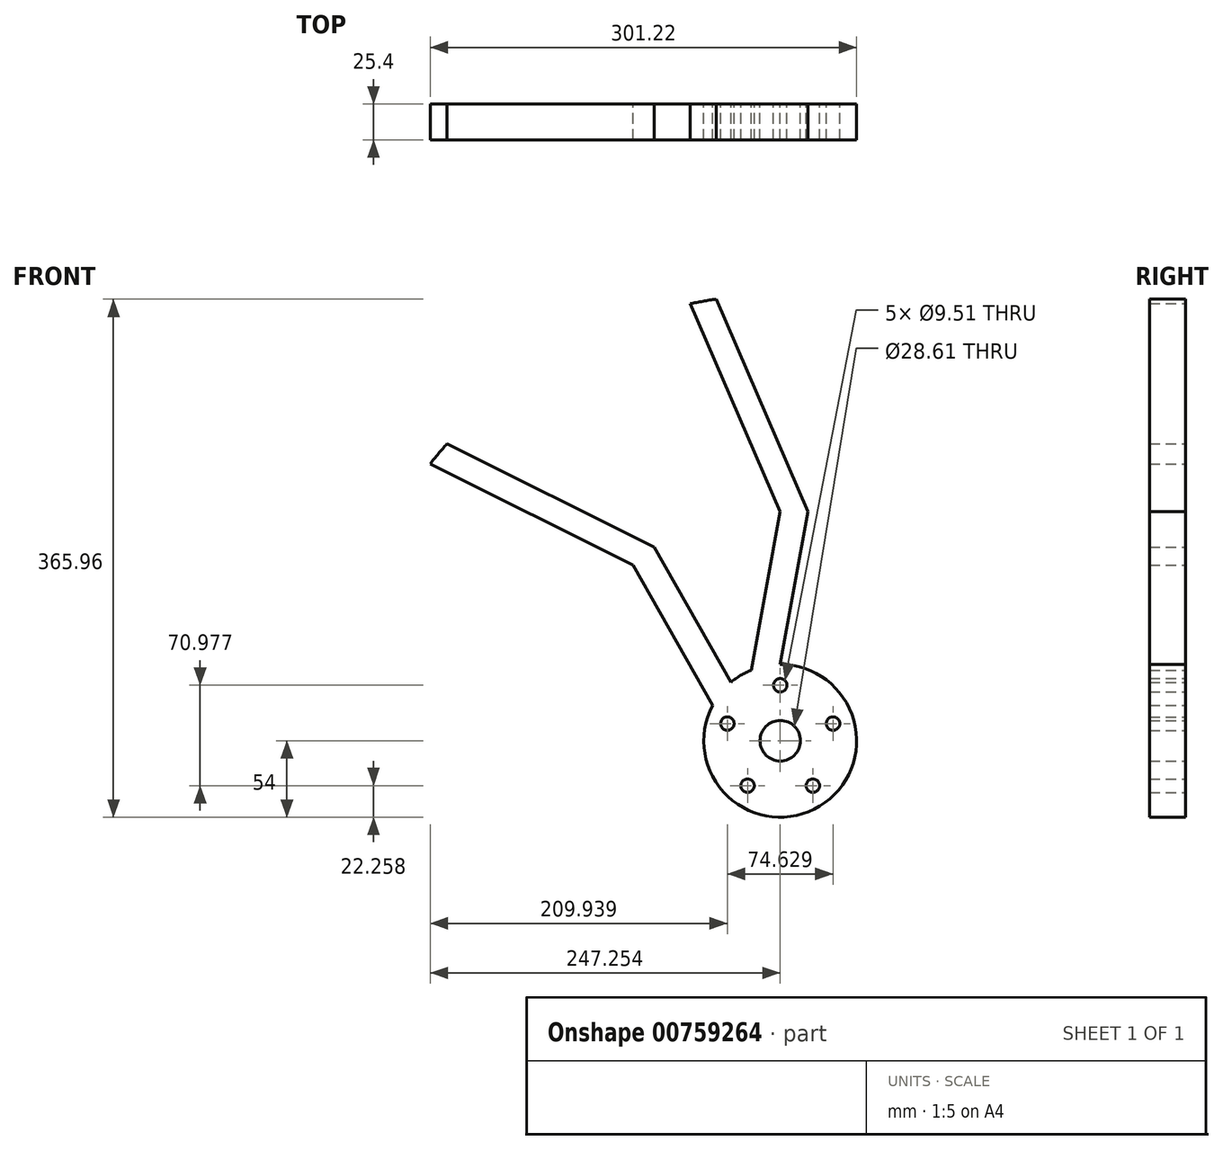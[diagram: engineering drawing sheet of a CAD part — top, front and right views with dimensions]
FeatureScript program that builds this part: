
annotation { "Feature Type Name" : "Feature", "Feature Type Description" : "" }
export const myFeature = defineFeature(function(context is Context, id is Id, definition is map)
    precondition{}
    {
        {
            var Q0;
            Q0=qCreatedBy(makeId("Front.planeOp"),FACE);
            var sketch = newSketch(context, id + "F0", { "sketchPlane" : qUnion([Q0])});
            skCircle(sketch, "E0", {"center": v(0, 0) * mm, "radius": 373.13 * mm});
            skCircle(sketch, "E1", {"center": v(0, 0) * mm, "radius": 315.24 * mm});
            skCircle(sketch, "E2", {"center": v(0, 0) * mm, "radius": 53.99 * mm});
            skLineSegment(sketch, "E3", {"start": v(-20.51, 49.94) * mm, "end": v(0, 161.87) * mm});
            skLineSegment(sketch, "E4", {"start": v(0, 161.87) * mm, "end": v(-63.68, 308.74) * mm});
            skLineSegment(sketch, "E5", {"start": v(0, 53.99) * mm, "end": v(19.77, 161.87) * mm});
            skLineSegment(sketch, "E6", {"start": v(19.77, 161.87) * mm, "end": v(-45.3, 311.97) * mm});
            skLineSegment(sketch, "E7.1.0", {"start": v(-104.05, 124) * mm, "end": v(-247.23, 195.58) * mm});
            skLineSegment(sketch, "E7.1.1", {"start": v(-47.82, 25.07) * mm, "end": v(-104.05, 124) * mm});
            skLineSegment(sketch, "E7.1.2", {"start": v(-34.7, 41.36) * mm, "end": v(-88.9, 136.7) * mm});
            skLineSegment(sketch, "E7.1.3", {"start": v(-88.9, 136.7) * mm, "end": v(-235.23, 209.86) * mm});
            skLineSegment(sketch, "E7.2.0", {"start": v(-159.4, 28.1) * mm, "end": v(-315.1, -9.1) * mm});
            skLineSegment(sketch, "E7.2.1", {"start": v(-52.74, -11.53) * mm, "end": v(-159.4, 28.1) * mm});
            skLineSegment(sketch, "E7.2.2", {"start": v(-53.17, 9.38) * mm, "end": v(-155.97, 47.58) * mm});
            skLineSegment(sketch, "E7.2.3", {"start": v(-155.97, 47.58) * mm, "end": v(-315.1, 9.56) * mm});
            skLineSegment(sketch, "E7.3.0", {"start": v(-140.18, -80.93) * mm, "end": v(-235.54, -209.52) * mm});
            skLineSegment(sketch, "E7.3.1", {"start": v(-33, -42.74) * mm, "end": v(-140.18, -80.93) * mm});
            skLineSegment(sketch, "E7.3.2", {"start": v(-46.76, -27) * mm, "end": v(-150.07, -63.8) * mm});
            skLineSegment(sketch, "E7.3.3", {"start": v(-150.07, -63.8) * mm, "end": v(-247.52, -195.22) * mm});
            skLineSegment(sketch, "E7.4.0", {"start": v(-55.36, -152.1) * mm, "end": v(-45.76, -311.9) * mm});
            skLineSegment(sketch, "E7.4.1", {"start": v(2.2, -53.94) * mm, "end": v(-55.36, -152.1) * mm});
            skLineSegment(sketch, "E7.4.2", {"start": v(-18.47, -50.73) * mm, "end": v(-73.94, -145.34) * mm});
            skLineSegment(sketch, "E7.4.3", {"start": v(-73.94, -145.34) * mm, "end": v(-64.13, -308.65) * mm});
            skLineSegment(sketch, "E7.5.0", {"start": v(55.36, -152.1) * mm, "end": v(165.43, -268.34) * mm});
            skLineSegment(sketch, "E7.5.1", {"start": v(36.36, -39.91) * mm, "end": v(55.36, -152.1) * mm});
            skLineSegment(sketch, "E7.5.2", {"start": v(18.47, -50.73) * mm, "end": v(36.78, -158.87) * mm});
            skLineSegment(sketch, "E7.5.3", {"start": v(36.78, -158.87) * mm, "end": v(149.27, -277.66) * mm});
            skLineSegment(sketch, "E7.6.0", {"start": v(140.18, -80.93) * mm, "end": v(299.22, -99.22) * mm});
            skLineSegment(sketch, "E7.6.1", {"start": v(53.5, -7.2) * mm, "end": v(140.18, -80.93) * mm});
            skLineSegment(sketch, "E7.6.2", {"start": v(46.76, -27) * mm, "end": v(130.3, -98.06) * mm});
            skLineSegment(sketch, "E7.6.3", {"start": v(130.3, -98.06) * mm, "end": v(292.82, -116.75) * mm});
            skLineSegment(sketch, "E7.7.0", {"start": v(159.4, 28.1) * mm, "end": v(293, 116.32) * mm});
            skLineSegment(sketch, "E7.7.1", {"start": v(45.62, 28.88) * mm, "end": v(159.4, 28.1) * mm});
            skLineSegment(sketch, "E7.7.2", {"start": v(53.17, 9.38) * mm, "end": v(162.84, 8.64) * mm});
            skLineSegment(sketch, "E7.7.3", {"start": v(162.84, 8.64) * mm, "end": v(299.36, 98.79) * mm});
            skLineSegment(sketch, "E7.8.0", {"start": v(104.05, 124) * mm, "end": v(149.68, 277.44) * mm});
            skLineSegment(sketch, "E7.8.1", {"start": v(16.38, 51.44) * mm, "end": v(104.05, 124) * mm});
            skLineSegment(sketch, "E7.8.2", {"start": v(34.7, 41.36) * mm, "end": v(119.2, 111.29) * mm});
            skLineSegment(sketch, "E7.8.3", {"start": v(119.2, 111.29) * mm, "end": v(165.82, 268.1) * mm});
            skCircle(sketch, "E8", {"center": v(0.02, 39.24) * mm, "radius": 4.75 * mm});
            skCircle(sketch, "E9.1.0", {"center": v(37.34, 12.13) * mm, "radius": 4.75 * mm});
            skCircle(sketch, "E9.2.0", {"center": v(23.09, -31.73) * mm, "radius": 4.75 * mm});
            skCircle(sketch, "E9.3.0", {"center": v(-23.04, -31.73) * mm, "radius": 4.75 * mm});
            skCircle(sketch, "E9.4.0", {"center": v(-37.3, 12.13) * mm, "radius": 4.75 * mm});
            skCircle(sketch, "E10", {"center": v(0.02, 0) * mm, "radius": 14.3 * mm});
            skSolve(sketch);
        }
        {
            var Q0;
            {var subQ1=sQuery(id+"F0.wireOp",EDGE,"E7.3.0");Q0=makeQuery(id+"F0.imprint","IMPRINT",FACE,{"disambiguationData":[TD([[makeQuery(id+"F0.imprint","IMPRINT",EDGE,{"derivedFrom":subQ1}),-1.0]])]});}
            var Q1;
            {var subQ0=sQuery(id+"F0.wireOp",EDGE,"E3");Q1=makeQuery(id+"F0.imprint","IMPRINT",FACE,{"disambiguationData":[TD([[makeQuery(id+"F0.imprint","IMPRINT",EDGE,{"derivedFrom":subQ0}),-1.0]])]});}
            var Q2;
            {var subQ0=sQuery(id+"F0.wireOp",EDGE,"E7.1.0");Q2=makeQuery(id+"F0.imprint","IMPRINT",FACE,{"disambiguationData":[TD([[makeQuery(id+"F0.imprint","IMPRINT",EDGE,{"derivedFrom":subQ0}),-1.0]])]});}
            var Q3;
            {var subQ0=sQuery(id+"F0.wireOp",EDGE,"E7.6.0");Q3=makeQuery(id+"F0.imprint","IMPRINT",FACE,{"disambiguationData":[TD([[makeQuery(id+"F0.imprint","IMPRINT",EDGE,{"derivedFrom":subQ0}),-1.0]])]});}
            var Q4;
            {var subQ1=sQuery(id+"F0.wireOp",EDGE,"E7.8.0");Q4=makeQuery(id+"F0.imprint","IMPRINT",FACE,{"disambiguationData":[TD([[makeQuery(id+"F0.imprint","IMPRINT",EDGE,{"derivedFrom":subQ1}),-1.0]])]});}
            var Q5;
            {var subQ0=sQuery(id+"F0.wireOp",EDGE,"E7.5.0");Q5=makeQuery(id+"F0.imprint","IMPRINT",FACE,{"disambiguationData":[TD([[makeQuery(id+"F0.imprint","IMPRINT",EDGE,{"derivedFrom":subQ0}),-1.0]])]});}
            var Q6;
            {var subQ3=sQuery(id+"F0.wireOp",EDGE,"E7.4.0");Q6=makeQuery(id+"F0.imprint","IMPRINT",FACE,{"disambiguationData":[TD([[makeQuery(id+"F0.imprint","IMPRINT",EDGE,{"derivedFrom":subQ3}),-1.0]])]});}
            var Q7;
            {var subQ0=sQuery(id+"F0.wireOp",EDGE,"E2");var subQ8=makeQuery(id+"F0.imprint","INTERSECT",VERTEX,{"derivedFrom":[subQ0,sQuery(id+"F0.wireOp",EDGE,"E7.7.1")]});Q7=makeQuery(id+"F0.imprint","IMPRINT",FACE,{"disambiguationData":[TD([[makeQuery(id+"F0.imprint","IMPRINT",EDGE,{"disambiguationData":[TD([[subQ8,1.0]])],"derivedFrom":subQ0}),1.0]])]});}
            var Q8;
            {var subQ0=sQuery(id+"F0.wireOp",EDGE,"E7.7.0");Q8=makeQuery(id+"F0.imprint","IMPRINT",FACE,{"disambiguationData":[TD([[makeQuery(id+"F0.imprint","IMPRINT",EDGE,{"derivedFrom":subQ0}),-1.0]])]});}
            var Q9;
            {var subQ1=sQuery(id+"F0.wireOp",EDGE,"E7.2.0");Q9=makeQuery(id+"F0.imprint","IMPRINT",FACE,{"disambiguationData":[TD([[makeQuery(id+"F0.imprint","IMPRINT",EDGE,{"derivedFrom":subQ1}),-1.0]])]});}
            extrude(context, id + "F1", {"entities" : qUnion([Q0, Q1, Q2, Q3, Q4, Q5, Q6, Q7, Q8, Q9]), "depth" : 25.4 * mm, "offsetDistance" : 25.4 * mm});
        }
    });
